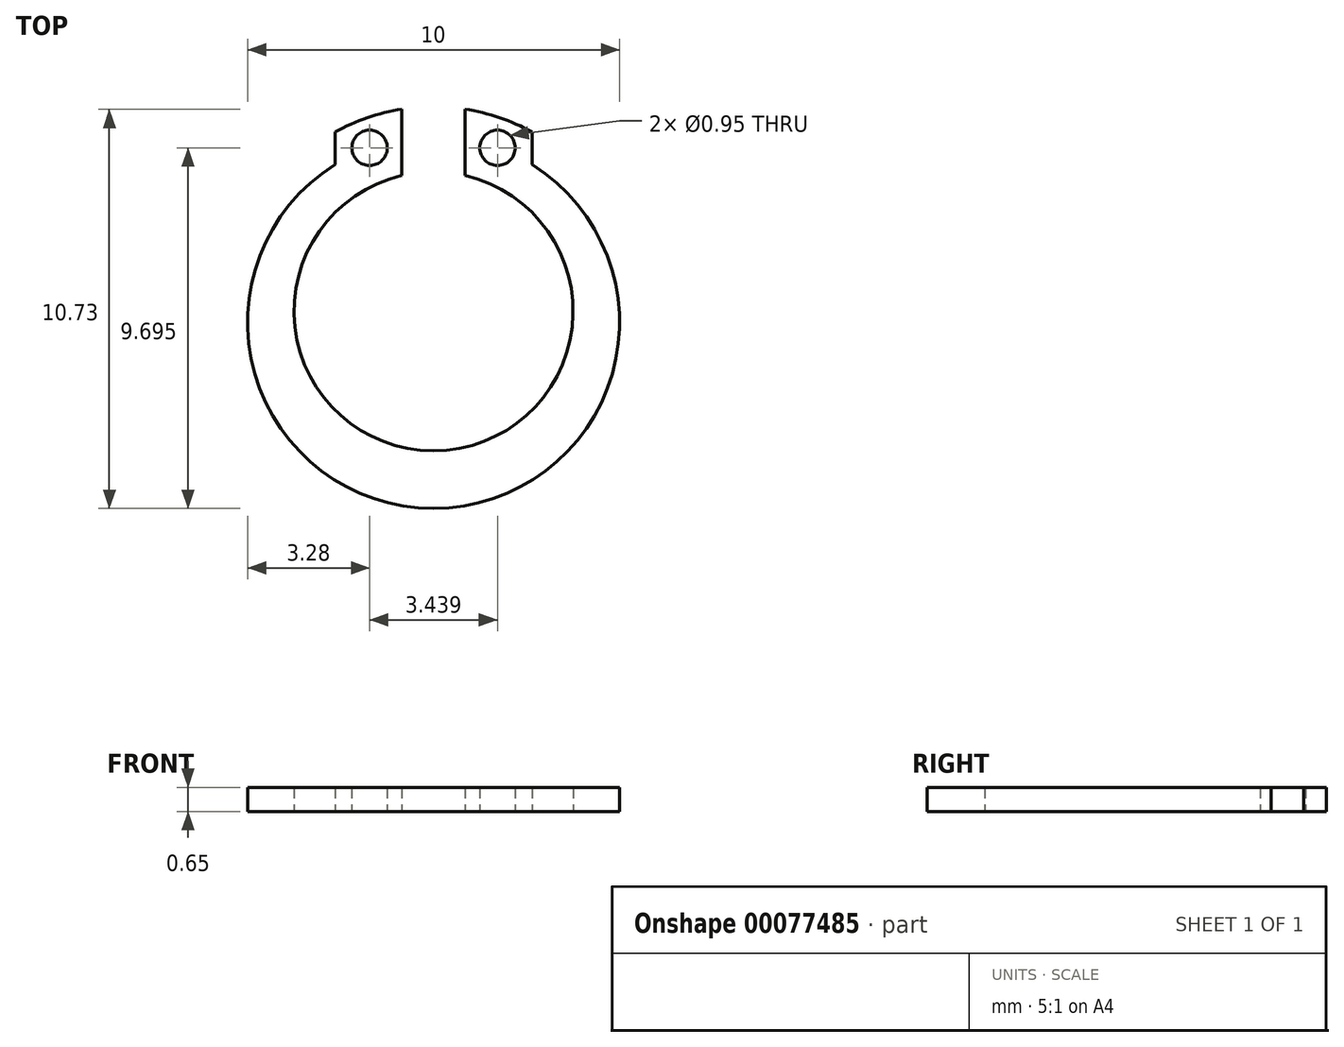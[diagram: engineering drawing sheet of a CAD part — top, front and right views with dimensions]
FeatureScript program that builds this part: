
annotation { "Feature Type Name" : "Feature", "Feature Type Description" : "" }
export const myFeature = defineFeature(function(context is Context, id is Id, definition is map)
    precondition{}
    {
        {
            var Q0;
            Q0=qCreatedBy(makeId("Top.planeOp"),FACE);
            var sketch = newSketch(context, id + "F0", { "sketchPlane" : qUnion([Q0])});
            skArc(sketch, "E0", {"start": v(-0.85, 5.43) * mm, "mid": v(-1.78, 5.2) * mm, "end": v(-2.65, 4.82) * mm});
            skLineSegment(sketch, "E1", {"start": v(0, 0) * mm, "end": v(0, -0.3) * mm, "construction": true});
            skArc(sketch, "E2", {"start": v(-0.85, 3.65) * mm, "mid": v(0, -3.75) * mm, "end": v(0.85, 3.65) * mm});
            skArc(sketch, "E3", {"start": v(-2.65, 3.94) * mm, "mid": v(0, -5.3) * mm, "end": v(2.65, 3.94) * mm});
            skLineSegment(sketch, "E4", {"start": v(-2.65, 4.82) * mm, "end": v(-2.65, 3.94) * mm});
            skLineSegment(sketch, "E5", {"start": v(2.65, 4.82) * mm, "end": v(2.65, 3.94) * mm});
            skLineSegment(sketch, "E6", {"start": v(0.85, 5.43) * mm, "end": v(0.85, 4.63) * mm});
            skLineSegment(sketch, "E7", {"start": v(-0.85, 5.43) * mm, "end": v(-0.85, 4.63) * mm});
            skLineSegment(sketch, "E8", {"start": v(-0.85, 4.63) * mm, "end": v(-0.85, 3.65) * mm});
            skLineSegment(sketch, "E9", {"start": v(0.85, 4.63) * mm, "end": v(0.85, 3.65) * mm});
            skArc(sketch, "E10.trimOffspring", {"start": v(2.65, 4.82) * mm, "mid": v(1.78, 5.2) * mm, "end": v(0.85, 5.43) * mm});
            skCircle(sketch, "E11", {"center": v(-1.72, 4.4) * mm, "radius": 0.47 * mm});
            skCircle(sketch, "E12", {"center": v(1.72, 4.4) * mm, "radius": 0.47 * mm});
            skSolve(sketch);
        }
        {
            var Q0;
            Q0=qSketchRegion(id+"F0",true);
            extrude(context, id + "F1", {"entities" : qUnion([Q0]), "depth" : 0.65 * mm});
        }
    });
